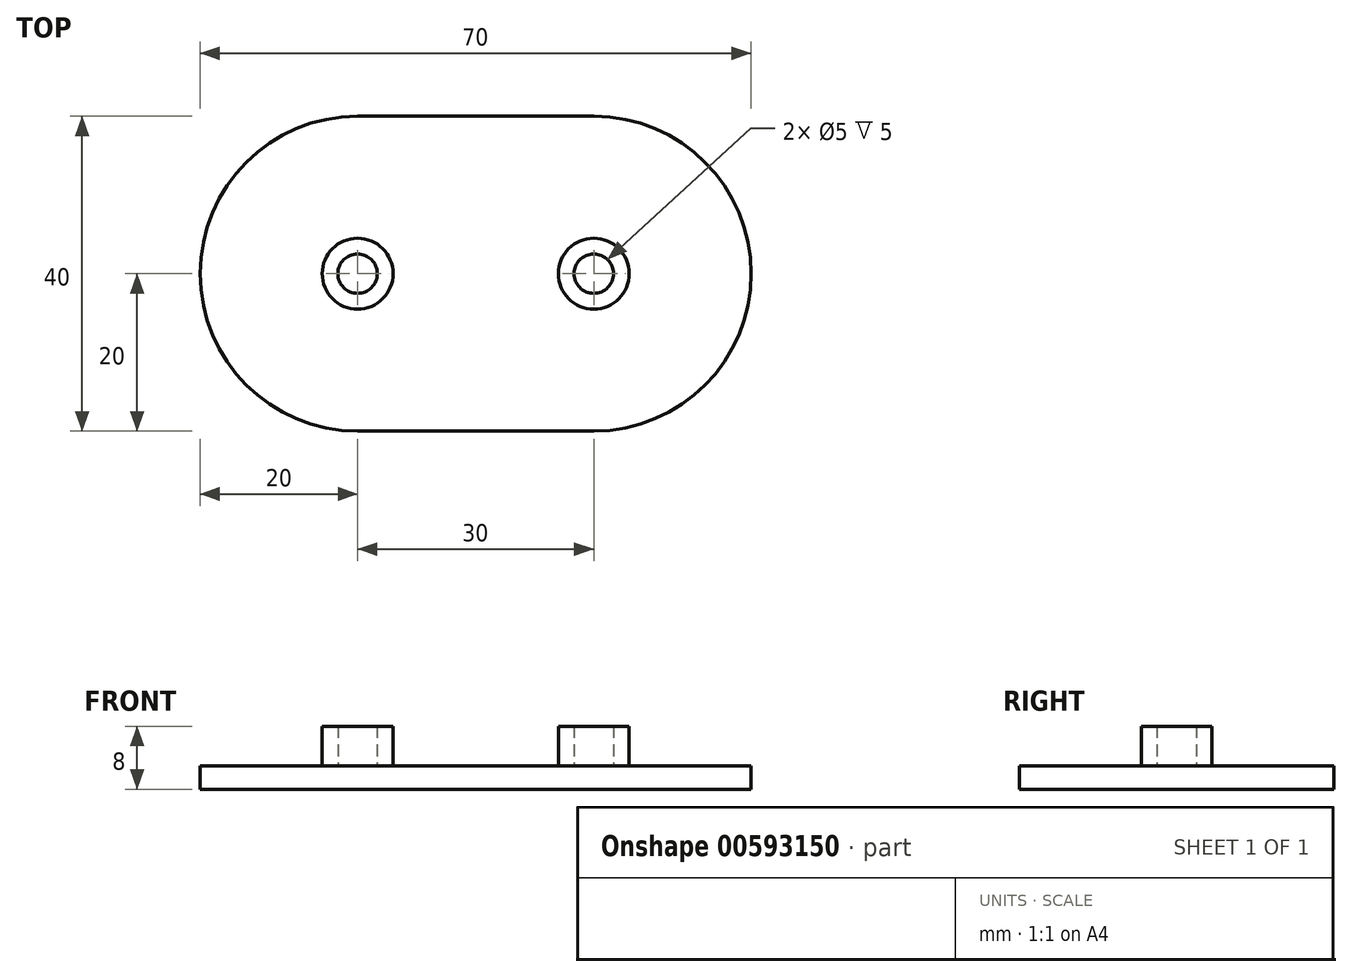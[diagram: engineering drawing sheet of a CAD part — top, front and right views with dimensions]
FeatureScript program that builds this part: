
annotation { "Feature Type Name" : "Feature", "Feature Type Description" : "" }
export const myFeature = defineFeature(function(context is Context, id is Id, definition is map)
    precondition{}
    {
        {
            var Q0;
            Q0=qCreatedBy(makeId("Top.planeOp"),FACE);
            var sketch = newSketch(context, id + "F0", { "sketchPlane" : qUnion([Q0])});
            skLineSegment(sketch, "E0.bottom", {"start": v(15, -20) * mm, "end": v(-15, -20) * mm});
            skLineSegment(sketch, "E0.top", {"start": v(15, 20) * mm, "end": v(-15, 20) * mm});
            skLineSegment(sketch, "E0.left", {"start": v(35, 0) * mm, "end": v(35, 0) * mm});
            skLineSegment(sketch, "E0.right", {"start": v(-35, 0) * mm, "end": v(-35, 0) * mm});
            skPoint(sketch, "E0.middle", {"position": v(0, 0) * mm});
            skPoint(sketch, "E1.visualSharp", {"position": v(-35, 20) * mm});
            skArc(sketch, "E1.filletArc", {"start": v(-15, 20) * mm, "mid": v(-29.14, 14.14) * mm, "end": v(-35, 0) * mm});
            skPoint(sketch, "E2.visualSharp", {"position": v(-35, -20) * mm});
            skArc(sketch, "E2.filletArc", {"start": v(-35, 0) * mm, "mid": v(-29.14, -14.14) * mm, "end": v(-15, -20) * mm});
            skPoint(sketch, "E3.visualSharp", {"position": v(35, -20) * mm});
            skArc(sketch, "E3.filletArc", {"start": v(15, -20) * mm, "mid": v(29.14, -14.14) * mm, "end": v(35, 0) * mm});
            skPoint(sketch, "E4.visualSharp", {"position": v(35, 20) * mm});
            skArc(sketch, "E4.filletArc", {"start": v(35, 0) * mm, "mid": v(29.14, 14.14) * mm, "end": v(15, 20) * mm});
            skSolve(sketch);
        }
        {
            var Q0;
            Q0 = qSketchRegion(id + "F0", true);
            extrude(context, id + "F1", {"entities" : qUnion([Q0]), "depth" : 3 * mm, "offsetDistance" : 25 * mm});
        }
        {
            var Q0;
            Q0=makeQuery(id+"F1.opExtrude","CAP_FACE",FACE,{"disambiguationData":[OSD([sQuery(id+"F0.wireOp",EDGE,"E0.bottom"),sQuery(id+"F0.wireOp",EDGE,"E0.top"),sQuery(id+"F0.wireOp",EDGE,"E1.filletArc"),sQuery(id+"F0.wireOp",EDGE,"E2.filletArc"),sQuery(id+"F0.wireOp",EDGE,"E3.filletArc"),sQuery(id+"F0.wireOp",EDGE,"E4.filletArc")])],"isStart":false});
            var sketch = newSketch(context, id + "F2", { "sketchPlane" : qUnion([Q0])});
            skCircle(sketch, "E5", {"center": v(-15, 0) * mm, "radius": 4.5 * mm});
            skCircle(sketch, "E6", {"center": v(15, 0) * mm, "radius": 4.5 * mm});
            skCircle(sketch, "E7", {"center": v(-15, 0) * mm, "radius": 2.5 * mm});
            skCircle(sketch, "E8", {"center": v(15, 0) * mm, "radius": 2.5 * mm});
            skSolve(sketch);
        }
        {
            var Q0;
            Q0 = qSketchRegion(id + "F2", true);
            extrude(context, id + "F3", {"entities" : qUnion([Q0]), "operationType" : NewBodyOperationType.ADD, "depth" : 5 * mm, "offsetDistance" : 25 * mm});
        }
    });
